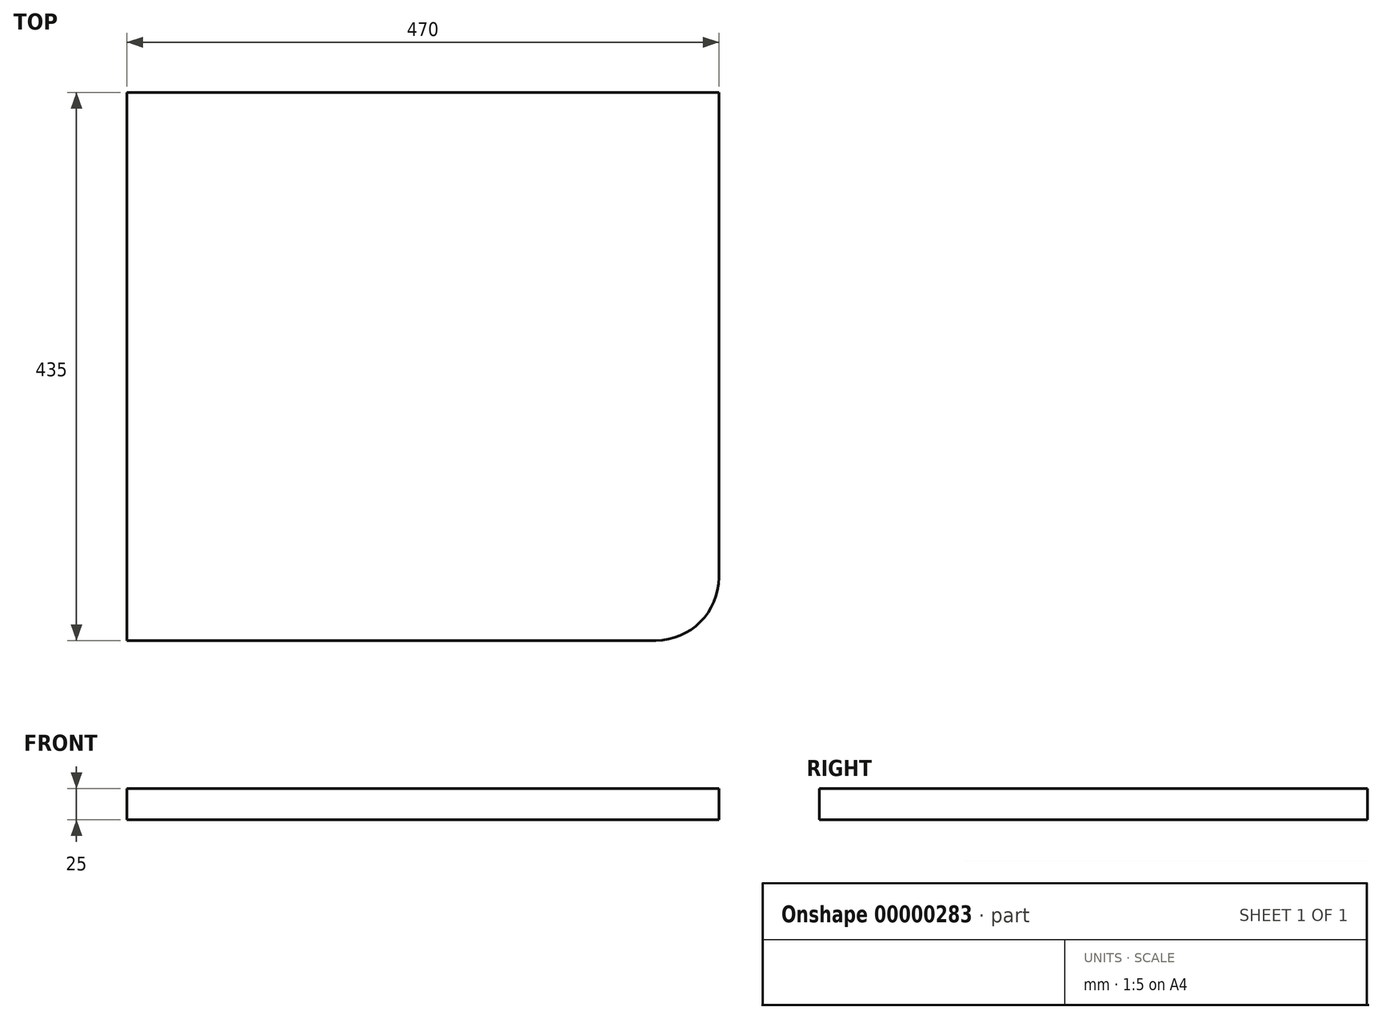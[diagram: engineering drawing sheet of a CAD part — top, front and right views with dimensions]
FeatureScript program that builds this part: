
annotation { "Feature Type Name" : "Feature", "Feature Type Description" : "" }
export const myFeature = defineFeature(function(context is Context, id is Id, definition is map)
    precondition{}
    {
        {
            var Q0;
            Q0=qCreatedBy(makeId("Top.planeOp"),FACE);
            var sketch = newSketch(context, id + "F0", { "sketchPlane" : qUnion([Q0])});
            skLineSegment(sketch, "E0.rect.bottom", {"start": v(235, -217.5) * mm, "end": v(-235, -217.5) * mm});
            skLineSegment(sketch, "E0.rect.top", {"start": v(235, 217.5) * mm, "end": v(-235, 217.5) * mm});
            skLineSegment(sketch, "E0.rect.left", {"start": v(235, -217.5) * mm, "end": v(235, 217.5) * mm});
            skLineSegment(sketch, "E0.rect.right", {"start": v(-235, -217.5) * mm, "end": v(-235, 217.5) * mm});
            skPoint(sketch, "E0.rect.middle", {"position": v(0, 0) * mm});
            skSolve(sketch);
        }
        {
            var Q0;
            Q0=makeQuery(id+"F0.imprint","IMPRINT",FACE,{"disambiguationData":[TD([[makeQuery(id+"F0.imprint","IMPRINT",EDGE,{"derivedFrom":sQuery(id+"F0.wireOp",EDGE,"E0.rect.bottom")}),-1.0]])]});
            extrude(context, id + "F1", {"entities" : qUnion([Q0]), "oppositeDirection" : true, "depth" : 25 * mm});
        }
        {
            var Q0;
            Q0=makeQuery(id+"F1.opExtrude","SWEPT_EDGE",EDGE,{"disambiguationData":[OSD([sQuery(id+"F0.wireOp",EDGE,"E0.rect.bottom"),sQuery(id+"F0.wireOp",EDGE,"E0.rect.left")])]});
            fillet(context, id + "F2", {"entities" : qUnion([Q0]), "radius" : 50 * mm, "tangentPropagation" : true, "allowEdgeOverflow" : false});
        }
    });
